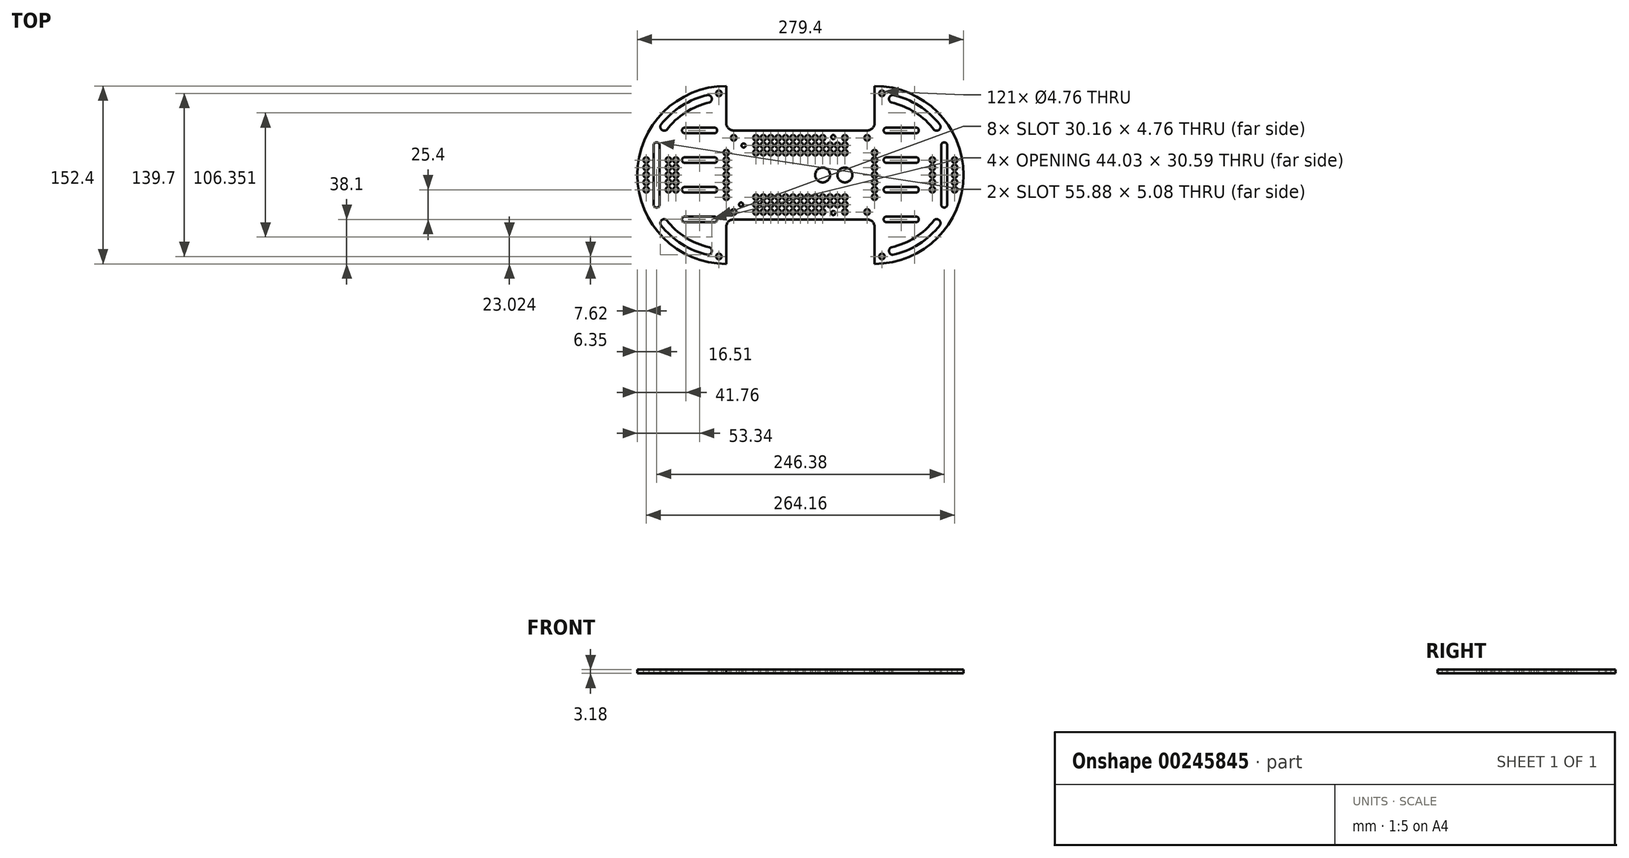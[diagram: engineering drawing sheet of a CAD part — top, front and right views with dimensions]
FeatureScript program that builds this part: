
annotation { "Feature Type Name" : "Feature", "Feature Type Description" : "" }
export const myFeature = defineFeature(function(context is Context, id is Id, definition is map)
    precondition{}
    {
        {
            var Q0;
            Q0=qCreatedBy(makeId("Top.planeOp"),FACE);
            var sketch = newSketch(context, id + "F0", { "sketchPlane" : qUnion([Q0])});
            skLineSegment(sketch, "E0.bottom", {"start": v(-57.15, 38.1) * mm, "end": v(57.15, 38.1) * mm});
            skLineSegment(sketch, "E0.top", {"start": v(-57.15, -38.1) * mm, "end": v(57.15, -38.1) * mm});
            skLineSegment(sketch, "E0.left", {"start": v(-63.5, 38.1) * mm, "end": v(-63.5, -38.1) * mm, "construction": true});
            skPoint(sketch, "E0.middle", {"position": v(0, 0) * mm});
            skLineSegment(sketch, "E1.bottom", {"start": v(-123.2, 27.94) * mm, "end": v(-123.19, 27.94) * mm});
            skLineSegment(sketch, "E1.top", {"start": v(-123.19, -27.94) * mm, "end": v(-123.19, -27.94) * mm});
            skLineSegment(sketch, "E1.left", {"start": v(-125.73, 25.4) * mm, "end": v(-125.73, -25.4) * mm});
            skLineSegment(sketch, "E1.right", {"start": v(-120.65, 25.4) * mm, "end": v(-120.65, -25.4) * mm});
            skPoint(sketch, "E2.visualSharp", {"position": v(-125.73, 27.94) * mm});
            skArc(sketch, "E2.filletArc", {"start": v(-123.2, 27.94) * mm, "mid": v(-124.99, 27.2) * mm, "end": v(-125.73, 25.4) * mm});
            skPoint(sketch, "E3.visualSharp", {"position": v(-120.65, 27.94) * mm});
            skArc(sketch, "E3.filletArc", {"start": v(-120.65, 25.4) * mm, "mid": v(-121.4, 27.2) * mm, "end": v(-123.19, 27.94) * mm});
            skPoint(sketch, "E4.visualSharp", {"position": v(-120.65, -27.94) * mm});
            skArc(sketch, "E4.filletArc", {"start": v(-123.19, -27.94) * mm, "mid": v(-121.4, -27.2) * mm, "end": v(-120.65, -25.4) * mm});
            skPoint(sketch, "E5.visualSharp", {"position": v(-125.73, -27.94) * mm});
            skArc(sketch, "E5.filletArc", {"start": v(-125.73, -25.4) * mm, "mid": v(-124.99, -27.2) * mm, "end": v(-123.19, -27.94) * mm});
            skPoint(sketch, "E6", {"position": v(-120.65, 0) * mm});
            skLineSegment(sketch, "E7", {"start": v(-120.65, 0) * mm, "end": v(-64.17, 0) * mm, "construction": true});
            skCircle(sketch, "E8", {"center": v(-57.82, -24.13) * mm, "radius": 1.59 * mm, "construction": true});
            skCircle(sketch, "E9", {"center": v(-56.55, 24.13) * mm, "radius": 1.59 * mm, "construction": true});
            skCircle(sketch, "E10", {"center": v(-5.75, 8.9) * mm, "radius": 1.59 * mm, "construction": true});
            skCircle(sketch, "E11", {"center": v(-5.75, -19.05) * mm, "radius": 1.59 * mm, "construction": true});
            skLineSegment(sketch, "E12", {"start": v(-57.82, -24.13) * mm, "end": v(-57.82, 24.13) * mm, "construction": true});
            skPoint(sketch, "E13", {"position": v(-57.82, 0) * mm});
            skCircle(sketch, "E14", {"center": v(-57.15, 31.75) * mm, "radius": 2.38 * mm});
            skCircle(sketch, "E15.0.1.0", {"center": v(-57.15, -31.75) * mm, "radius": 2.38 * mm});
            skCircle(sketch, "E15.1.0.0", {"center": v(57.15, 31.75) * mm, "radius": 2.38 * mm});
            skCircle(sketch, "E15.1.1.0", {"center": v(57.15, -31.75) * mm, "radius": 2.38 * mm});
            skCircle(sketch, "E16", {"center": v(-132.08, 12.7) * mm, "radius": 2.38 * mm});
            skCircle(sketch, "E17", {"center": v(-132.08, 0) * mm, "radius": 2.38 * mm});
            skCircle(sketch, "E18", {"center": v(-132.08, 6.35) * mm, "radius": 2.38 * mm});
            skLineSegment(sketch, "E19", {"start": v(-132.08, 12.7) * mm, "end": v(-132.08, 6.35) * mm, "construction": true});
            skLineSegment(sketch, "E20", {"start": v(-132.08, 0) * mm, "end": v(-132.08, 6.35) * mm, "construction": true});
            skCircle(sketch, "E21", {"center": v(-132.08, -6.35) * mm, "radius": 2.38 * mm});
            skLineSegment(sketch, "E22", {"start": v(-132.08, 0) * mm, "end": v(-132.08, -6.35) * mm, "construction": true});
            skCircle(sketch, "E23", {"center": v(-132.08, -12.7) * mm, "radius": 2.38 * mm});
            skLineSegment(sketch, "E24", {"start": v(-132.08, -6.35) * mm, "end": v(-132.08, -12.7) * mm, "construction": true});
            skCircle(sketch, "E25", {"center": v(-38.1, 31.75) * mm, "radius": 2.38 * mm});
            skCircle(sketch, "E26.0.1.0", {"center": v(-38.1, 25.4) * mm, "radius": 2.38 * mm});
            skCircle(sketch, "E26.0.2.0", {"center": v(-38.1, 19.05) * mm, "radius": 2.38 * mm});
            skCircle(sketch, "E26.1.0.0", {"center": v(-31.75, 31.75) * mm, "radius": 2.38 * mm});
            skCircle(sketch, "E26.1.1.0", {"center": v(-31.75, 25.4) * mm, "radius": 2.38 * mm});
            skCircle(sketch, "E26.1.2.0", {"center": v(-31.75, 19.05) * mm, "radius": 2.38 * mm});
            skCircle(sketch, "E26.2.0.0", {"center": v(-25.4, 31.75) * mm, "radius": 2.38 * mm});
            skCircle(sketch, "E26.2.1.0", {"center": v(-25.4, 25.4) * mm, "radius": 2.38 * mm});
            skCircle(sketch, "E26.2.2.0", {"center": v(-25.4, 19.05) * mm, "radius": 2.38 * mm});
            skCircle(sketch, "E26.3.0.0", {"center": v(-19.05, 31.75) * mm, "radius": 2.38 * mm});
            skCircle(sketch, "E26.3.1.0", {"center": v(-19.05, 25.4) * mm, "radius": 2.38 * mm});
            skCircle(sketch, "E26.3.2.0", {"center": v(-19.05, 19.05) * mm, "radius": 2.38 * mm});
            skCircle(sketch, "E26.4.0.0", {"center": v(-12.7, 31.75) * mm, "radius": 2.38 * mm});
            skCircle(sketch, "E26.4.1.0", {"center": v(-12.7, 25.4) * mm, "radius": 2.38 * mm});
            skCircle(sketch, "E26.5.0.0", {"center": v(-6.35, 31.75) * mm, "radius": 2.38 * mm});
            skCircle(sketch, "E26.5.1.0", {"center": v(-6.35, 25.4) * mm, "radius": 2.38 * mm});
            skCircle(sketch, "E26.6.0.0", {"center": v(0, 31.75) * mm, "radius": 2.38 * mm});
            skCircle(sketch, "E26.6.1.0", {"center": v(0, 25.4) * mm, "radius": 2.38 * mm});
            skCircle(sketch, "E26.7.0.0", {"center": v(6.35, 31.75) * mm, "radius": 2.38 * mm});
            skCircle(sketch, "E26.7.1.0", {"center": v(6.35, 25.4) * mm, "radius": 2.38 * mm});
            skCircle(sketch, "E26.7.2.0", {"center": v(6.35, 19.05) * mm, "radius": 2.38 * mm});
            skCircle(sketch, "E26.8.0.0", {"center": v(12.7, 31.75) * mm, "radius": 2.38 * mm});
            skCircle(sketch, "E26.8.1.0", {"center": v(12.7, 25.4) * mm, "radius": 2.38 * mm});
            skCircle(sketch, "E26.8.2.0", {"center": v(12.7, 19.05) * mm, "radius": 2.38 * mm});
            skCircle(sketch, "E26.9.0.0", {"center": v(19.05, 31.75) * mm, "radius": 2.38 * mm});
            skCircle(sketch, "E26.9.1.0", {"center": v(19.05, 25.4) * mm, "radius": 2.38 * mm});
            skCircle(sketch, "E26.9.2.0", {"center": v(19.05, 19.05) * mm, "radius": 2.38 * mm});
            skCircle(sketch, "E26.10.1.0", {"center": v(25.4, 25.4) * mm, "radius": 2.38 * mm});
            skCircle(sketch, "E26.10.2.0", {"center": v(25.4, 19.05) * mm, "radius": 2.38 * mm});
            skCircle(sketch, "E26.11.1.0", {"center": v(31.75, 25.4) * mm, "radius": 2.38 * mm});
            skCircle(sketch, "E26.11.2.0", {"center": v(31.75, 19.05) * mm, "radius": 2.38 * mm});
            skCircle(sketch, "E26.12.0.0", {"center": v(38.1, 31.75) * mm, "radius": 2.38 * mm});
            skCircle(sketch, "E26.12.1.0", {"center": v(38.1, 25.4) * mm, "radius": 2.38 * mm});
            skCircle(sketch, "E26.12.2.0", {"center": v(38.1, 19.05) * mm, "radius": 2.38 * mm});
            skLineSegment(sketch, "E26.direction1", {"start": v(-38.1, 31.75) * mm, "end": v(-31.75, 31.75) * mm, "construction": true});
            skLineSegment(sketch, "E26.direction2", {"start": v(-38.1, 25.4) * mm, "end": v(-38.1, 31.75) * mm, "construction": true});
            skCircle(sketch, "E27", {"center": v(-38.1, -31.75) * mm, "radius": 2.38 * mm});
            skCircle(sketch, "E28.0.1.0", {"center": v(-38.1, -25.4) * mm, "radius": 2.38 * mm});
            skCircle(sketch, "E28.0.2.0", {"center": v(-38.1, -19.05) * mm, "radius": 2.38 * mm});
            skCircle(sketch, "E28.1.0.0", {"center": v(-31.75, -31.75) * mm, "radius": 2.38 * mm});
            skCircle(sketch, "E28.1.1.0", {"center": v(-31.75, -25.4) * mm, "radius": 2.38 * mm});
            skCircle(sketch, "E28.1.2.0", {"center": v(-31.75, -19.05) * mm, "radius": 2.38 * mm});
            skCircle(sketch, "E28.2.0.0", {"center": v(-25.4, -31.75) * mm, "radius": 2.38 * mm});
            skCircle(sketch, "E28.2.1.0", {"center": v(-25.4, -25.4) * mm, "radius": 2.38 * mm});
            skCircle(sketch, "E28.2.2.0", {"center": v(-25.4, -19.05) * mm, "radius": 2.38 * mm});
            skCircle(sketch, "E28.3.0.0", {"center": v(-19.05, -31.75) * mm, "radius": 2.38 * mm});
            skCircle(sketch, "E28.3.1.0", {"center": v(-19.05, -25.4) * mm, "radius": 2.38 * mm});
            skCircle(sketch, "E28.3.2.0", {"center": v(-19.05, -19.05) * mm, "radius": 2.38 * mm});
            skCircle(sketch, "E28.4.0.0", {"center": v(-12.7, -31.75) * mm, "radius": 2.38 * mm});
            skCircle(sketch, "E28.5.0.0", {"center": v(-6.35, -31.75) * mm, "radius": 2.38 * mm});
            skCircle(sketch, "E28.6.0.0", {"center": v(0, -31.75) * mm, "radius": 2.38 * mm});
            skCircle(sketch, "E28.7.0.0", {"center": v(6.35, -31.75) * mm, "radius": 2.38 * mm});
            skCircle(sketch, "E28.7.1.0", {"center": v(6.35, -25.4) * mm, "radius": 2.38 * mm});
            skCircle(sketch, "E28.7.2.0", {"center": v(6.35, -19.05) * mm, "radius": 2.38 * mm});
            skCircle(sketch, "E28.8.0.0", {"center": v(12.7, -31.75) * mm, "radius": 2.38 * mm});
            skCircle(sketch, "E28.8.1.0", {"center": v(12.7, -25.4) * mm, "radius": 2.38 * mm});
            skCircle(sketch, "E28.8.2.0", {"center": v(12.7, -19.05) * mm, "radius": 2.38 * mm});
            skCircle(sketch, "E28.9.0.0", {"center": v(19.05, -31.75) * mm, "radius": 2.38 * mm});
            skCircle(sketch, "E28.9.1.0", {"center": v(19.05, -25.4) * mm, "radius": 2.38 * mm});
            skCircle(sketch, "E28.9.2.0", {"center": v(19.05, -19.05) * mm, "radius": 2.38 * mm});
            skCircle(sketch, "E28.10.1.0", {"center": v(25.4, -25.4) * mm, "radius": 2.38 * mm});
            skCircle(sketch, "E28.10.2.0", {"center": v(25.4, -19.05) * mm, "radius": 2.38 * mm});
            skCircle(sketch, "E28.11.1.0", {"center": v(31.75, -25.4) * mm, "radius": 2.38 * mm});
            skCircle(sketch, "E28.11.2.0", {"center": v(31.75, -19.05) * mm, "radius": 2.38 * mm});
            skCircle(sketch, "E28.12.0.0", {"center": v(38.1, -31.75) * mm, "radius": 2.38 * mm});
            skCircle(sketch, "E28.12.1.0", {"center": v(38.1, -25.4) * mm, "radius": 2.38 * mm});
            skCircle(sketch, "E28.12.2.0", {"center": v(38.1, -19.05) * mm, "radius": 2.38 * mm});
            skLineSegment(sketch, "E28.direction1", {"start": v(-38.1, -31.75) * mm, "end": v(-31.75, -31.75) * mm, "construction": true});
            skLineSegment(sketch, "E28.direction2", {"start": v(-38.1, -31.75) * mm, "end": v(-38.1, -25.4) * mm, "construction": true});
            skCircle(sketch, "E29.MirrorC", {"center": v(132.08, 12.7) * mm, "radius": 2.38 * mm});
            skArc(sketch, "E30.MirrorCS", {"start": v(123.2, 27.94) * mm, "mid": v(124.99, 27.2) * mm, "end": v(125.73, 25.4) * mm});
            skLineSegment(sketch, "E31.MirrorCS", {"start": v(120.65, 25.4) * mm, "end": v(120.65, -25.4) * mm});
            skArc(sketch, "E32.MirrorCS", {"start": v(123.19, -27.94) * mm, "mid": v(121.4, -27.2) * mm, "end": v(120.65, -25.4) * mm});
            skCircle(sketch, "E33.MirrorC", {"center": v(132.08, 6.35) * mm, "radius": 2.38 * mm});
            skCircle(sketch, "E34.MirrorC", {"center": v(132.08, -12.7) * mm, "radius": 2.38 * mm});
            skLineSegment(sketch, "E35.MirrorCS", {"start": v(125.73, 25.4) * mm, "end": v(125.73, -25.4) * mm});
            skArc(sketch, "E36.MirrorCS", {"start": v(120.65, 25.4) * mm, "mid": v(121.4, 27.2) * mm, "end": v(123.19, 27.94) * mm});
            skArc(sketch, "E37.MirrorCS", {"start": v(125.73, -25.4) * mm, "mid": v(124.99, -27.2) * mm, "end": v(123.19, -27.94) * mm});
            skCircle(sketch, "E38.MirrorC", {"center": v(132.08, 0) * mm, "radius": 2.38 * mm});
            skCircle(sketch, "E39.MirrorC", {"center": v(132.08, -6.35) * mm, "radius": 2.38 * mm});
            skCircle(sketch, "E40", {"center": v(-63.5, 19.05) * mm, "radius": 2.38 * mm});
            skCircle(sketch, "E41.0.1.0", {"center": v(-63.5, 12.7) * mm, "radius": 2.38 * mm});
            skCircle(sketch, "E41.0.2.0", {"center": v(-63.5, 6.35) * mm, "radius": 2.38 * mm});
            skCircle(sketch, "E41.0.3.0", {"center": v(-63.5, 0) * mm, "radius": 2.38 * mm});
            skCircle(sketch, "E41.0.4.0", {"center": v(-63.5, -6.35) * mm, "radius": 2.38 * mm});
            skCircle(sketch, "E41.0.5.0", {"center": v(-63.5, -12.7) * mm, "radius": 2.38 * mm});
            skCircle(sketch, "E41.0.6.0", {"center": v(-63.5, -19.05) * mm, "radius": 2.38 * mm});
            skLineSegment(sketch, "E41.direction1", {"start": v(-63.5, 19.05) * mm, "end": v(-38.1, 19.05) * mm, "construction": true});
            skLineSegment(sketch, "E41.direction2", {"start": v(-63.5, 19.05) * mm, "end": v(-63.5, 12.7) * mm, "construction": true});
            skCircle(sketch, "E42.MirrorC", {"center": v(63.5, 0) * mm, "radius": 2.38 * mm});
            skCircle(sketch, "E43.MirrorC", {"center": v(63.5, 19.05) * mm, "radius": 2.38 * mm});
            skCircle(sketch, "E44.MirrorC", {"center": v(63.5, -12.7) * mm, "radius": 2.38 * mm});
            skCircle(sketch, "E45.MirrorC", {"center": v(63.5, -6.35) * mm, "radius": 2.38 * mm});
            skCircle(sketch, "E46.MirrorC", {"center": v(63.5, -19.05) * mm, "radius": 2.38 * mm});
            skCircle(sketch, "E47.MirrorC", {"center": v(63.5, 12.7) * mm, "radius": 2.38 * mm});
            skCircle(sketch, "E48.MirrorC", {"center": v(63.5, 6.35) * mm, "radius": 2.38 * mm});
            skLineSegment(sketch, "E49", {"start": v(-63.5, 44.45) * mm, "end": v(-63.5, 76.2) * mm});
            skLineSegment(sketch, "E50", {"start": v(-63.5, -44.45) * mm, "end": v(-63.5, -76.2) * mm});
            skArc(sketch, "E51", {"start": v(-63.5, 76.2) * mm, "mid": v(-139.7, 0) * mm, "end": v(-63.5, -76.2) * mm});
            skLineSegment(sketch, "E52", {"start": v(-63.5, -76.2) * mm, "end": v(-50.05, -76.2) * mm, "construction": true});
            skLineSegment(sketch, "E53.MirrorCS", {"start": v(63.5, -44.45) * mm, "end": v(63.5, -76.2) * mm});
            skArc(sketch, "E54.MirrorCS", {"start": v(63.5, 76.2) * mm, "mid": v(139.7, 0) * mm, "end": v(63.5, -76.2) * mm});
            skLineSegment(sketch, "E55.MirrorCS", {"start": v(63.5, 44.45) * mm, "end": v(63.5, 76.2) * mm});
            skPoint(sketch, "E56.visualSharp", {"position": v(-63.5, -38.1) * mm});
            skArc(sketch, "E56.filletArc", {"start": v(-57.15, -38.1) * mm, "mid": v(-61.64, -39.96) * mm, "end": v(-63.5, -44.45) * mm});
            skPoint(sketch, "E57.visualSharp", {"position": v(63.5, -38.1) * mm});
            skArc(sketch, "E57.filletArc", {"start": v(63.5, -44.45) * mm, "mid": v(61.64, -39.96) * mm, "end": v(57.15, -38.1) * mm});
            skPoint(sketch, "E58.visualSharp", {"position": v(-63.5, 38.1) * mm});
            skArc(sketch, "E58.filletArc", {"start": v(-63.5, 44.45) * mm, "mid": v(-61.64, 39.96) * mm, "end": v(-57.15, 38.1) * mm});
            skPoint(sketch, "E59.visualSharp", {"position": v(63.5, 38.1) * mm});
            skArc(sketch, "E59.filletArc", {"start": v(57.15, 38.1) * mm, "mid": v(61.64, 39.96) * mm, "end": v(63.5, 44.45) * mm});
            skCircle(sketch, "E60", {"center": v(-69.85, 69.85) * mm, "radius": 2.38 * mm});
            skLineSegment(sketch, "E61", {"start": v(-63.5, 76.2) * mm, "end": v(-79.1, 76.2) * mm, "construction": true});
            skCircle(sketch, "E62.0.1.0", {"center": v(-69.85, -69.85) * mm, "radius": 2.38 * mm});
            skCircle(sketch, "E62.1.0.0", {"center": v(69.85, 69.85) * mm, "radius": 2.38 * mm});
            skCircle(sketch, "E62.1.1.0", {"center": v(69.85, -69.85) * mm, "radius": 2.38 * mm});
            skLineSegment(sketch, "E62.direction1", {"start": v(-69.85, 69.85) * mm, "end": v(69.85, 69.85) * mm, "construction": true});
            skLineSegment(sketch, "E62.direction2", {"start": v(-69.85, 69.85) * mm, "end": v(-69.85, -69.85) * mm, "construction": true});
            skCircle(sketch, "E63.1.0.0", {"center": v(-113.03, -12.7) * mm, "radius": 2.38 * mm});
            skCircle(sketch, "E63.1.0.1", {"center": v(-113.03, 12.7) * mm, "radius": 2.38 * mm});
            skCircle(sketch, "E63.1.0.2", {"center": v(-113.03, 6.35) * mm, "radius": 2.38 * mm});
            skCircle(sketch, "E63.1.0.3", {"center": v(-113.03, 0) * mm, "radius": 2.38 * mm});
            skCircle(sketch, "E63.1.0.4", {"center": v(-113.03, -6.35) * mm, "radius": 2.38 * mm});
            skLineSegment(sketch, "E63.direction1", {"start": v(-132.08, -12.7) * mm, "end": v(-113.03, -12.7) * mm, "construction": true});
            skArc(sketch, "E64", {"start": v(-79.1, -68.47) * mm, "mid": v(-101.6, -59.25) * mm, "end": v(-119.58, -42.9) * mm});
            skArc(sketch, "E65", {"start": v(-114.7, -38.45) * mm, "mid": v(-98.4, -53.48) * mm, "end": v(-77.93, -62) * mm});
            skArc(sketch, "E66", {"start": v(73.66, 40.48) * mm, "mid": v(71.28, 38.1) * mm, "end": v(73.66, 35.72) * mm});
            skLineSegment(sketch, "E67", {"start": v(73.66, 40.48) * mm, "end": v(99.06, 40.48) * mm});
            skLineSegment(sketch, "E68", {"start": v(73.66, 35.72) * mm, "end": v(99.06, 35.72) * mm});
            skArc(sketch, "E69", {"start": v(99.06, 40.48) * mm, "mid": v(101.44, 38.1) * mm, "end": v(99.06, 35.72) * mm});
            skArc(sketch, "E70", {"start": v(-114.7, -38.45) * mm, "mid": v(-118.9, -38.76) * mm, "end": v(-119.58, -42.9) * mm});
            skPoint(sketch, "E71.orphan", {"position": v(-122.76, -38.45) * mm});
            skArc(sketch, "E72", {"start": v(-79.1, -68.47) * mm, "mid": v(-75.94, -65.7) * mm, "end": v(-77.93, -62) * mm});
            skArc(sketch, "E73.MirrorCS", {"start": v(-79.1, 68.47) * mm, "mid": v(-75.94, 65.7) * mm, "end": v(-77.93, 62) * mm});
            skArc(sketch, "E74.MirrorCS", {"start": v(-114.7, 38.45) * mm, "mid": v(-98.4, 53.48) * mm, "end": v(-77.93, 62) * mm});
            skArc(sketch, "E75.MirrorCS", {"start": v(-114.7, 38.45) * mm, "mid": v(-118.9, 38.76) * mm, "end": v(-119.58, 42.9) * mm});
            skArc(sketch, "E76.MirrorCS", {"start": v(-79.1, 68.47) * mm, "mid": v(-101.6, 59.25) * mm, "end": v(-119.58, 42.9) * mm});
            skArc(sketch, "E77.MirrorCS", {"start": v(114.7, 38.45) * mm, "mid": v(98.4, 53.48) * mm, "end": v(77.93, 62) * mm});
            skArc(sketch, "E78.MirrorCS", {"start": v(79.1, -68.47) * mm, "mid": v(101.6, -59.25) * mm, "end": v(119.58, -42.9) * mm});
            skArc(sketch, "E79.MirrorCS", {"start": v(114.7, 38.45) * mm, "mid": v(118.9, 38.76) * mm, "end": v(119.58, 42.9) * mm});
            skArc(sketch, "E80.MirrorCS", {"start": v(114.7, -38.45) * mm, "mid": v(118.9, -38.76) * mm, "end": v(119.58, -42.9) * mm});
            skArc(sketch, "E81.MirrorCS", {"start": v(79.1, -68.47) * mm, "mid": v(75.94, -65.7) * mm, "end": v(77.93, -62) * mm});
            skArc(sketch, "E82.MirrorCS", {"start": v(79.1, 68.47) * mm, "mid": v(101.6, 59.25) * mm, "end": v(119.58, 42.9) * mm});
            skArc(sketch, "E83.MirrorCS", {"start": v(114.7, -38.45) * mm, "mid": v(98.4, -53.48) * mm, "end": v(77.93, -62) * mm});
            skArc(sketch, "E84.MirrorCS", {"start": v(79.1, 68.47) * mm, "mid": v(75.94, 65.7) * mm, "end": v(77.93, 62) * mm});
            skArc(sketch, "E85.0.1.0", {"start": v(73.66, 15.08) * mm, "mid": v(71.28, 12.7) * mm, "end": v(73.66, 10.32) * mm});
            skLineSegment(sketch, "E85.0.1.1", {"start": v(73.66, 10.32) * mm, "end": v(99.06, 10.32) * mm});
            skArc(sketch, "E85.0.1.2", {"start": v(99.06, 15.08) * mm, "mid": v(101.44, 12.7) * mm, "end": v(99.06, 10.32) * mm});
            skLineSegment(sketch, "E85.0.1.3", {"start": v(73.66, 15.08) * mm, "end": v(99.06, 15.08) * mm});
            skArc(sketch, "E85.0.2.0", {"start": v(73.66, -10.32) * mm, "mid": v(71.28, -12.7) * mm, "end": v(73.66, -15.08) * mm});
            skLineSegment(sketch, "E85.0.2.1", {"start": v(73.66, -15.08) * mm, "end": v(99.06, -15.08) * mm});
            skArc(sketch, "E85.0.2.2", {"start": v(99.06, -10.32) * mm, "mid": v(101.44, -12.7) * mm, "end": v(99.06, -15.08) * mm});
            skLineSegment(sketch, "E85.0.2.3", {"start": v(73.66, -10.32) * mm, "end": v(99.06, -10.32) * mm});
            skArc(sketch, "E85.0.3.0", {"start": v(73.66, -35.72) * mm, "mid": v(71.28, -38.1) * mm, "end": v(73.66, -40.48) * mm});
            skLineSegment(sketch, "E85.0.3.1", {"start": v(73.66, -40.48) * mm, "end": v(99.06, -40.48) * mm});
            skArc(sketch, "E85.0.3.2", {"start": v(99.06, -35.72) * mm, "mid": v(101.44, -38.1) * mm, "end": v(99.06, -40.48) * mm});
            skLineSegment(sketch, "E85.0.3.3", {"start": v(73.66, -35.72) * mm, "end": v(99.06, -35.72) * mm});
            skLineSegment(sketch, "E86.MirrorCS", {"start": v(-73.66, -15.08) * mm, "end": v(-99.06, -15.08) * mm});
            skArc(sketch, "E87.MirrorCS", {"start": v(-99.06, 15.08) * mm, "mid": v(-101.44, 12.7) * mm, "end": v(-99.06, 10.32) * mm});
            skLineSegment(sketch, "E88.MirrorCS", {"start": v(-73.66, -35.72) * mm, "end": v(-99.06, -35.72) * mm});
            skLineSegment(sketch, "E89.MirrorCS", {"start": v(-73.66, 40.48) * mm, "end": v(-99.06, 40.48) * mm});
            skLineSegment(sketch, "E90.MirrorCS", {"start": v(-73.66, -10.32) * mm, "end": v(-99.06, -10.32) * mm});
            skArc(sketch, "E91.MirrorCS", {"start": v(-99.06, 40.48) * mm, "mid": v(-101.44, 38.1) * mm, "end": v(-99.06, 35.72) * mm});
            skArc(sketch, "E92.MirrorCS", {"start": v(-73.66, -10.32) * mm, "mid": v(-71.28, -12.7) * mm, "end": v(-73.66, -15.08) * mm});
            skLineSegment(sketch, "E93.MirrorCS", {"start": v(-73.66, -40.48) * mm, "end": v(-99.06, -40.48) * mm});
            skLineSegment(sketch, "E94.MirrorCS", {"start": v(-73.66, 10.32) * mm, "end": v(-99.06, 10.32) * mm});
            skArc(sketch, "E95.MirrorCS", {"start": v(-99.06, -35.72) * mm, "mid": v(-101.44, -38.1) * mm, "end": v(-99.06, -40.48) * mm});
            skArc(sketch, "E96.MirrorCS", {"start": v(-73.66, 40.48) * mm, "mid": v(-71.28, 38.1) * mm, "end": v(-73.66, 35.72) * mm});
            skArc(sketch, "E97.MirrorCS", {"start": v(-99.06, -10.32) * mm, "mid": v(-101.44, -12.7) * mm, "end": v(-99.06, -15.08) * mm});
            skLineSegment(sketch, "E98.MirrorCS", {"start": v(-73.66, 35.72) * mm, "end": v(-99.06, 35.72) * mm});
            skLineSegment(sketch, "E99.MirrorCS", {"start": v(-73.66, 15.08) * mm, "end": v(-99.06, 15.08) * mm});
            skArc(sketch, "E100.MirrorCS", {"start": v(-73.66, -35.72) * mm, "mid": v(-71.28, -38.1) * mm, "end": v(-73.66, -40.48) * mm});
            skArc(sketch, "E101.MirrorCS", {"start": v(-73.66, 15.08) * mm, "mid": v(-71.28, 12.7) * mm, "end": v(-73.66, 10.32) * mm});
            skCircle(sketch, "E102", {"center": v(19.05, 0) * mm, "radius": 6.35 * mm});
            skCircle(sketch, "E103", {"center": v(38.1, 0) * mm, "radius": 6.35 * mm});
            skCircle(sketch, "E104.MirrorC", {"center": v(113.03, -12.7) * mm, "radius": 2.38 * mm});
            skCircle(sketch, "E105.MirrorC", {"center": v(113.03, -6.35) * mm, "radius": 2.38 * mm});
            skCircle(sketch, "E106.MirrorC", {"center": v(113.03, 0) * mm, "radius": 2.38 * mm});
            skCircle(sketch, "E107.MirrorC", {"center": v(113.03, 6.35) * mm, "radius": 2.38 * mm});
            skCircle(sketch, "E108.MirrorC", {"center": v(113.03, 12.7) * mm, "radius": 2.38 * mm});
            skCircle(sketch, "E109.1.0.0", {"center": v(-106.68, -6.35) * mm, "radius": 2.38 * mm});
            skCircle(sketch, "E109.1.0.1", {"center": v(-106.68, 0) * mm, "radius": 2.38 * mm});
            skCircle(sketch, "E109.1.0.2", {"center": v(-106.68, 6.35) * mm, "radius": 2.38 * mm});
            skCircle(sketch, "E109.1.0.3", {"center": v(-106.68, 12.7) * mm, "radius": 2.38 * mm});
            skCircle(sketch, "E109.1.0.4", {"center": v(-106.68, -12.7) * mm, "radius": 2.38 * mm});
            skLineSegment(sketch, "E109.direction1", {"start": v(-113.03, -12.7) * mm, "end": v(-106.68, -12.7) * mm, "construction": true});
            skPoint(sketch, "E110.middle", {"position": v(49.4, 15.17) * mm});
            skCircle(sketch, "E111", {"center": v(28.16, 32.42) * mm, "radius": 1.75 * mm});
            skCircle(sketch, "E112", {"center": v(28.16, -32.58) * mm, "radius": 1.75 * mm});
            skCircle(sketch, "E113", {"center": v(-50.8, -25.4) * mm, "radius": 1.75 * mm});
            skCircle(sketch, "E114.1.0.0", {"center": v(-12.7, -25.4) * mm, "radius": 2.38 * mm});
            skCircle(sketch, "E114.1.0.1", {"center": v(-12.7, 19.05) * mm, "radius": 2.38 * mm});
            skCircle(sketch, "E114.1.0.2", {"center": v(-12.7, -19.05) * mm, "radius": 2.38 * mm});
            skCircle(sketch, "E114.2.0.0", {"center": v(-6.35, -25.4) * mm, "radius": 2.38 * mm});
            skCircle(sketch, "E114.2.0.1", {"center": v(-6.35, 19.05) * mm, "radius": 2.38 * mm});
            skCircle(sketch, "E114.2.0.2", {"center": v(-6.35, -19.05) * mm, "radius": 2.38 * mm});
            skCircle(sketch, "E114.3.0.0", {"center": v(0, -25.4) * mm, "radius": 2.38 * mm});
            skCircle(sketch, "E114.3.0.1", {"center": v(0, 19.05) * mm, "radius": 2.38 * mm});
            skCircle(sketch, "E114.3.0.2", {"center": v(0, -19.05) * mm, "radius": 2.38 * mm});
            skLineSegment(sketch, "E114.direction1", {"start": v(-19.05, -25.4) * mm, "end": v(-12.7, -25.4) * mm, "construction": true});
            skCircle(sketch, "E115", {"center": v(-48.65, 25.23) * mm, "radius": 1.75 * mm});
            skSolve(sketch);
        }
        {
            var Q0;
            Q0=makeQuery(id+"F0.imprint","IMPRINT",FACE,{"disambiguationData":[TD([[makeQuery(id+"F0.imprint","IMPRINT",EDGE,{"derivedFrom":sQuery(id+"F0.wireOp",EDGE,"E0.bottom")}),-1.0]])]});
            extrude(context, id + "F1", {"entities" : qUnion([Q0]), "depth" : 3.17 * mm});
        }
    });
